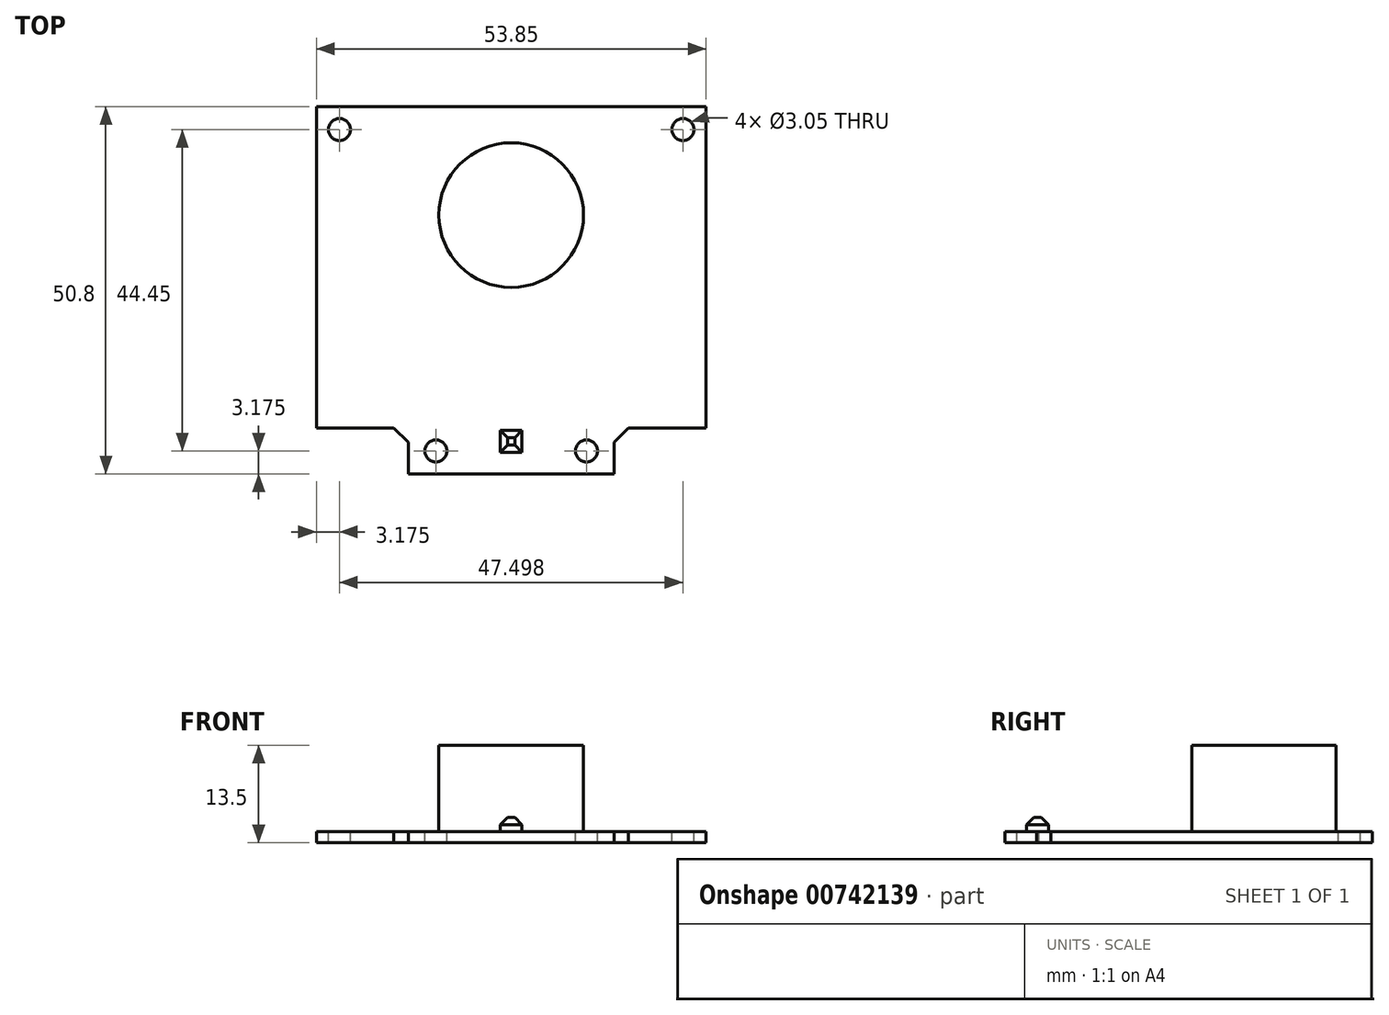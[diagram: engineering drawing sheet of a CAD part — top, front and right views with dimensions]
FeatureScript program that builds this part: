
annotation { "Feature Type Name" : "Feature", "Feature Type Description" : "" }
export const myFeature = defineFeature(function(context is Context, id is Id, definition is map)
    precondition{}
    {
        {
            var Q0;
            Q0=qCreatedBy(makeId("Top.planeOp"),FACE);
            var sketch = newSketch(context, id + "F0", { "sketchPlane" : qUnion([Q0])});
            skLineSegment(sketch, "E0.bottom", {"start": v(12.7, -6.35) * mm, "end": v(41.15, -6.35) * mm});
            skLineSegment(sketch, "E0.top", {"start": v(0, 44.45) * mm, "end": v(53.85, 44.45) * mm});
            skLineSegment(sketch, "E0.left", {"start": v(0, 0) * mm, "end": v(0, 44.45) * mm});
            skLineSegment(sketch, "E0.right", {"start": v(53.85, 0) * mm, "end": v(53.85, 44.45) * mm});
            skLineSegment(sketch, "E1.top", {"start": v(0, 0) * mm, "end": v(10.7, 0) * mm});
            skLineSegment(sketch, "E1.right", {"start": v(12.7, -6.35) * mm, "end": v(12.7, -2) * mm});
            skLineSegment(sketch, "E2.top", {"start": v(53.85, 0) * mm, "end": v(43.15, 0) * mm});
            skLineSegment(sketch, "E2.right", {"start": v(41.15, -6.35) * mm, "end": v(41.15, -2) * mm});
            skLineSegment(sketch, "E3", {"start": v(10.7, 0) * mm, "end": v(12.7, -2) * mm});
            skPoint(sketch, "E4.orphan", {"position": v(12.7, 0) * mm});
            skLineSegment(sketch, "E5", {"start": v(41.15, -2) * mm, "end": v(43.15, 0) * mm});
            skPoint(sketch, "E6.orphan", {"position": v(53.85, -6.35) * mm});
            skSolve(sketch);
        }
        {
            var Q0;
            Q0=makeQuery(id+"F0.imprint","IMPRINT",FACE,{"disambiguationData":[TD([[makeQuery(id+"F0.imprint","IMPRINT",EDGE,{"derivedFrom":sQuery(id+"F0.wireOp",EDGE,"E0.bottom")}),1.0]])]});
            extrude(context, id + "F1", {"entities" : qUnion([Q0]), "depth" : 1.5 * mm, "offsetDistance" : 25 * mm});
        }
        {
            var Q0;
            Q0=makeQuery(id+"F1.opExtrude","CAP_FACE",FACE,{"disambiguationData":[OSD([sQuery(id+"F0.wireOp",EDGE,"E0.bottom"),sQuery(id+"F0.wireOp",EDGE,"E0.top"),sQuery(id+"F0.wireOp",EDGE,"E0.left"),sQuery(id+"F0.wireOp",EDGE,"E0.right"),sQuery(id+"F0.wireOp",EDGE,"E1.top"),sQuery(id+"F0.wireOp",EDGE,"E1.right"),sQuery(id+"F0.wireOp",EDGE,"E2.top"),sQuery(id+"F0.wireOp",EDGE,"E2.right"),sQuery(id+"F0.wireOp",EDGE,"E3"),sQuery(id+"F0.wireOp",EDGE,"E5")])],"isStart":false});
            var sketch = newSketch(context, id + "F2", { "sketchPlane" : qUnion([Q0])});
            skCircle(sketch, "E7", {"center": v(3.17, 41.27) * mm, "radius": 1.52 * mm});
            skCircle(sketch, "E8", {"center": v(16.5, -3.17) * mm, "radius": 1.52 * mm});
            skCircle(sketch, "E9", {"center": v(37.34, -3.17) * mm, "radius": 1.52 * mm});
            skCircle(sketch, "E10", {"center": v(50.67, 41.27) * mm, "radius": 1.52 * mm});
            skSolve(sketch);
        }
        {
            var Q0;
            Q0=makeQuery(id+"F2.imprint","IMPRINT",FACE,{"disambiguationData":[TD([[makeQuery(id+"F2.imprint","IMPRINT",EDGE,{"derivedFrom":sQuery(id+"F2.wireOp",EDGE,"E7")}),1.0]])]});
            var Q1;
            Q1=makeQuery(id+"F2.imprint","IMPRINT",FACE,{"disambiguationData":[TD([[makeQuery(id+"F2.imprint","IMPRINT",EDGE,{"derivedFrom":sQuery(id+"F2.wireOp",EDGE,"E10")}),1.0]])]});
            var Q2;
            Q2=makeQuery(id+"F2.imprint","IMPRINT",FACE,{"disambiguationData":[TD([[makeQuery(id+"F2.imprint","IMPRINT",EDGE,{"derivedFrom":sQuery(id+"F2.wireOp",EDGE,"E8")}),1.0]])]});
            var Q3;
            Q3=makeQuery(id+"F2.imprint","IMPRINT",FACE,{"disambiguationData":[TD([[makeQuery(id+"F2.imprint","IMPRINT",EDGE,{"derivedFrom":sQuery(id+"F2.wireOp",EDGE,"E9")}),1.0]])]});
            extrude(context, id + "F3", {"entities" : qUnion([Q0, Q1, Q2, Q3]), "operationType" : NewBodyOperationType.REMOVE, "oppositeDirection" : true, "depth" : 25 * mm, "offsetDistance" : 25 * mm});
        }
        {
            var Q0;
            Q0=makeQuery(id+"F1.opExtrude","CAP_FACE",FACE,{"disambiguationData":[OSD([sQuery(id+"F0.wireOp",EDGE,"E0.bottom"),sQuery(id+"F0.wireOp",EDGE,"E0.top"),sQuery(id+"F0.wireOp",EDGE,"E0.left"),sQuery(id+"F0.wireOp",EDGE,"E0.right"),sQuery(id+"F0.wireOp",EDGE,"E1.top"),sQuery(id+"F0.wireOp",EDGE,"E1.right"),sQuery(id+"F0.wireOp",EDGE,"E2.top"),sQuery(id+"F0.wireOp",EDGE,"E2.right"),sQuery(id+"F0.wireOp",EDGE,"E3"),sQuery(id+"F0.wireOp",EDGE,"E5")])],"isStart":false});
            var sketch = newSketch(context, id + "F4", { "sketchPlane" : qUnion([Q0])});
            skSolve(sketch);
        }
        {
            var Q0;
            Q0=makeQuery(id+"F4.imprint","IMPRINT",FACE,{"disambiguationData":[TD([[makeQuery(id+"F4.imprint","IMPRINT",EDGE,{"derivedFrom":makeQuery(id+"F1.opExtrude","CAP_EDGE",EDGE,{"disambiguationData":[OSD([sQuery(id+"F0.wireOp",EDGE,"E0.bottom")])],"isStart":false})}),1.0]])]});
            var sketch = newSketch(context, id + "F5", { "sketchPlane" : qUnion([Q0])});
            skCircle(sketch, "E11", {"center": v(26.92, 29.45) * mm, "radius": 10 * mm});
            skLineSegment(sketch, "E12.0.0", {"start": v(53.85, 44.45) * mm, "end": v(0, 44.45) * mm});
            skLineSegment(sketch, "E12.0.1", {"start": v(0, 44.45) * mm, "end": v(0, 0) * mm});
            skLineSegment(sketch, "E12.0.2", {"start": v(0, 0) * mm, "end": v(10.7, 0) * mm});
            skLineSegment(sketch, "E12.0.3", {"start": v(10.7, 0) * mm, "end": v(12.7, -2) * mm});
            skLineSegment(sketch, "E12.0.4", {"start": v(12.7, -2) * mm, "end": v(12.7, -6.35) * mm});
            skLineSegment(sketch, "E12.0.5", {"start": v(12.7, -6.35) * mm, "end": v(41.15, -6.35) * mm});
            skLineSegment(sketch, "E12.0.6", {"start": v(41.15, -6.35) * mm, "end": v(41.15, -2) * mm});
            skLineSegment(sketch, "E12.0.7", {"start": v(41.15, -2) * mm, "end": v(43.15, 0) * mm});
            skLineSegment(sketch, "E12.0.8", {"start": v(43.15, 0) * mm, "end": v(53.85, 0) * mm});
            skLineSegment(sketch, "E12.0.9", {"start": v(53.85, 0) * mm, "end": v(53.85, 44.45) * mm});
            skLineSegment(sketch, "E13", {"start": v(26.92, 29.45) * mm, "end": v(53.85, 44.45) * mm, "construction": true});
            skLineSegment(sketch, "E14", {"start": v(0, 44.45) * mm, "end": v(26.92, 29.45) * mm, "construction": true});
            skSolve(sketch);
        }
        {
            var Q0;
            Q0=makeQuery(id+"F5.imprint","IMPRINT",FACE,{"disambiguationData":[TD([[makeQuery(id+"F5.imprint","IMPRINT",EDGE,{"derivedFrom":sQuery(id+"F5.wireOp",EDGE,"E11")}),1.0]])]});
            extrude(context, id + "F6", {"entities" : qUnion([Q0]), "operationType" : NewBodyOperationType.ADD, "depth" : 12 * mm, "offsetDistance" : 25 * mm});
        }
        {
            var Q0;
            Q0=makeQuery(id+"F4.imprint","IMPRINT",FACE,{"disambiguationData":[TD([[makeQuery(id+"F4.imprint","IMPRINT",EDGE,{"derivedFrom":makeQuery(id+"F1.opExtrude","CAP_EDGE",EDGE,{"disambiguationData":[OSD([sQuery(id+"F0.wireOp",EDGE,"E0.bottom")])],"isStart":false})}),1.0]])]});
            var sketch = newSketch(context, id + "F7", { "sketchPlane" : qUnion([Q0])});
            skLineSegment(sketch, "E15.bottom", {"start": v(25.42, -0.35) * mm, "end": v(28.42, -0.35) * mm});
            skLineSegment(sketch, "E15.top", {"start": v(25.42, -3.35) * mm, "end": v(28.42, -3.35) * mm});
            skLineSegment(sketch, "E15.left", {"start": v(25.42, -0.35) * mm, "end": v(25.42, -3.35) * mm});
            skLineSegment(sketch, "E15.right", {"start": v(28.42, -0.35) * mm, "end": v(28.42, -3.35) * mm});
            skLineSegment(sketch, "E16", {"start": v(26.92, -3.35) * mm, "end": v(26.92, -6.35) * mm, "construction": true});
            skSolve(sketch);
        }
        {
            var Q0;
            Q0=makeQuery(id+"F7.imprint","IMPRINT",FACE,{"disambiguationData":[TD([[makeQuery(id+"F7.imprint","IMPRINT",EDGE,{"derivedFrom":sQuery(id+"F7.wireOp",EDGE,"E15.bottom")}),-1.0]])]});
            extrude(context, id + "F8", {"entities" : qUnion([Q0]), "operationType" : NewBodyOperationType.ADD, "depth" : 2 * mm, "offsetDistance" : 25 * mm});
        }
        {
            var Q0;
            Q0=makeQuery(id+"F8.opExtrude","CAP_EDGE",EDGE,{"disambiguationData":[OSD([sQuery(id+"F7.wireOp",EDGE,"E15.bottom")])],"isStart":false});
            var Q1;
            Q1=makeQuery(id+"F8.opExtrude","CAP_EDGE",EDGE,{"disambiguationData":[OSD([sQuery(id+"F7.wireOp",EDGE,"E15.left")])],"isStart":false});
            var Q2;
            Q2=makeQuery(id+"F8.opExtrude","CAP_EDGE",EDGE,{"disambiguationData":[OSD([sQuery(id+"F7.wireOp",EDGE,"E15.right")])],"isStart":false});
            var Q3;
            Q3=makeQuery(id+"F8.opExtrude","CAP_EDGE",EDGE,{"disambiguationData":[OSD([sQuery(id+"F7.wireOp",EDGE,"E15.top")])],"isStart":false});
            chamfer(context, id + "F9", {"entities" : qUnion([Q0, Q1, Q2, Q3]), "width" : 1 * mm, "tangentPropagation" : true});
        }
    });
